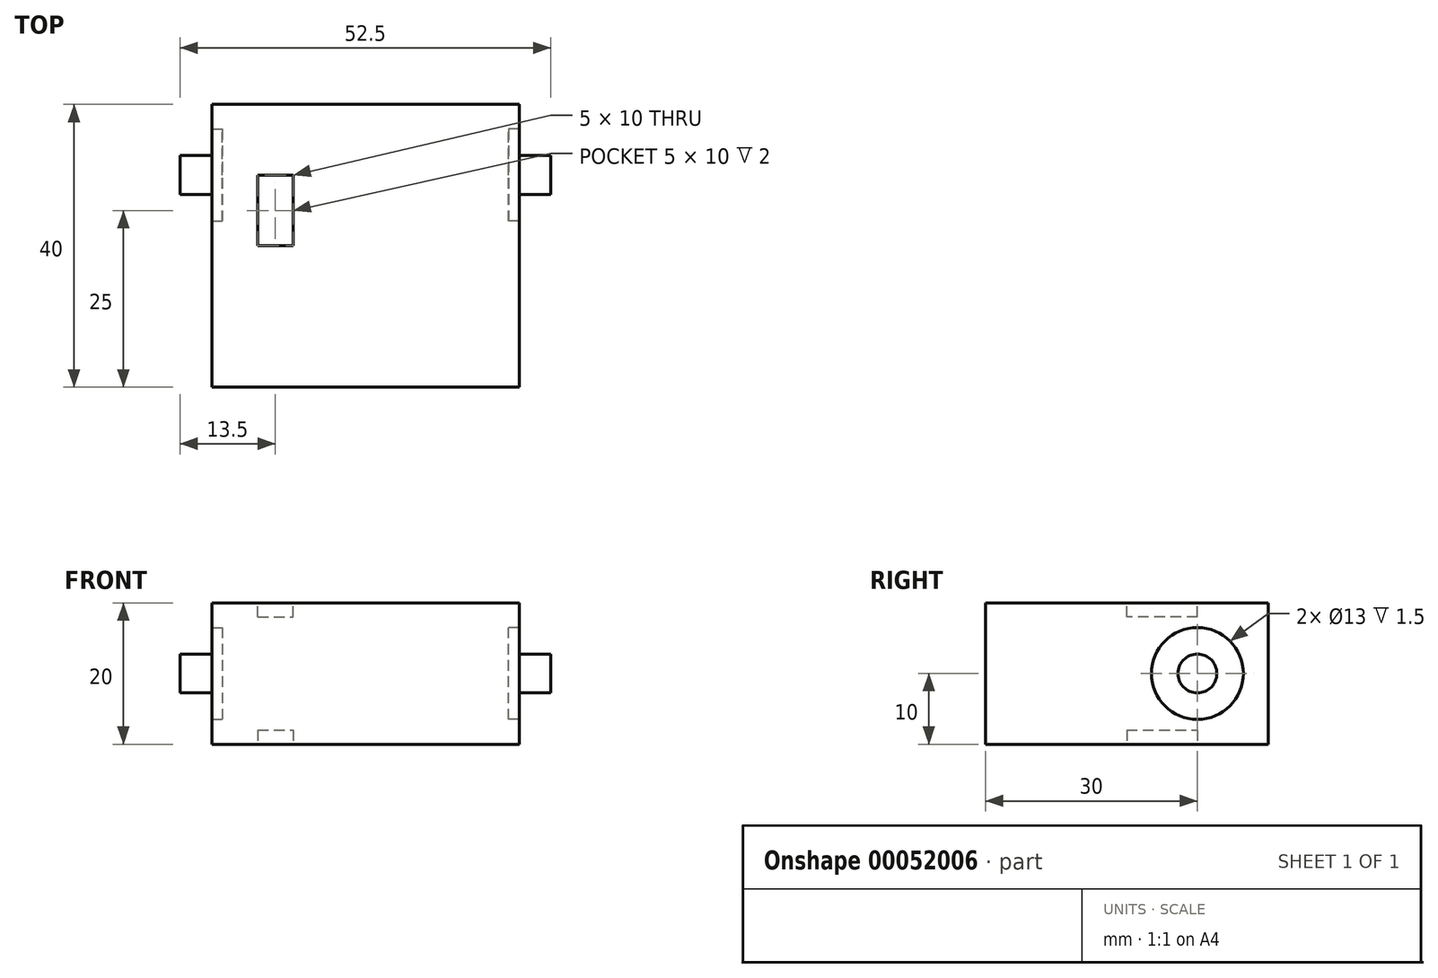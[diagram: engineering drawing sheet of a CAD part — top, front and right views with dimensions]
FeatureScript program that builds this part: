
annotation { "Feature Type Name" : "Feature", "Feature Type Description" : "" }
export const myFeature = defineFeature(function(context is Context, id is Id, definition is map)
    precondition{}
    {
        {
            var Q0;
            Q0=qCreatedBy(makeId("Top.planeOp"),FACE);
            var sketch = newSketch(context, id + "F0", { "sketchPlane" : qUnion([Q0])});
            skLineSegment(sketch, "E0.bottom", {"start": v(-20.25, 20) * mm, "end": v(20.25, 20) * mm});
            skLineSegment(sketch, "E0.top", {"start": v(-20.25, -20) * mm, "end": v(20.25, -20) * mm});
            skLineSegment(sketch, "E0.left", {"start": v(-20.25, 20) * mm, "end": v(-20.25, -20) * mm});
            skLineSegment(sketch, "E0.right", {"start": v(20.25, 20) * mm, "end": v(20.25, -20) * mm});
            skSolve(sketch);
        }
        {
            var Q0;
            Q0=makeQuery(id+"F0.imprint","IMPRINT",FACE,{"disambiguationData":[TD([[makeQuery(id+"F0.imprint","IMPRINT",EDGE,{"derivedFrom":sQuery(id+"F0.wireOp",EDGE,"E0.bottom")}),-1.0]])]});
            extrude(context, id + "F1", {"entities" : qUnion([Q0]), "endBound" : BoundingType.SYMMETRIC, "oppositeDirection" : true, "depth" : 20 * mm, "offsetDistance" : 25 * mm});
        }
        {
            var Q0;
            Q0=makeQuery(id+"F1.opExtrude","SWEPT_FACE",FACE,{"disambiguationData":[OSD([sQuery(id+"F0.wireOp",EDGE,"E0.left")])]});
            var sketch = newSketch(context, id + "F2", { "sketchPlane" : qUnion([Q0])});
            skLineSegment(sketch, "E1.bottom", {"start": v(-20, 10) * mm, "end": v(-10, 10) * mm});
            skLineSegment(sketch, "E1.top", {"start": v(-20, -10) * mm, "end": v(-10, -10) * mm});
            skLineSegment(sketch, "E1.left", {"start": v(-20, 10) * mm, "end": v(-20, -10) * mm});
            skLineSegment(sketch, "E1.right", {"start": v(-10, 10) * mm, "end": v(-10, -10) * mm});
            skPoint(sketch, "E2", {"position": v(-10, 0) * mm});
            skCircle(sketch, "E3", {"center": v(-10, 0) * mm, "radius": 6.5 * mm});
            skSolve(sketch);
        }
        {
            var Q0;
            {var subQ0=sQuery(id+"F2.wireOp",EDGE,"E3");var subQ1=sQuery(id+"F2.wireOp",EDGE,"E1.right");var subQ2=makeQuery(id+"F2.imprint","INTERSECT",VERTEX,{"disambiguationData":[OD(0.0)],"derivedFrom":[subQ1,subQ0]});Q0=makeQuery(id+"F2.imprint","IMPRINT",FACE,{"disambiguationData":[TD([[makeQuery(id+"F2.imprint","IMPRINT",EDGE,{"disambiguationData":[TD([[subQ2,-1.0]])],"derivedFrom":subQ1}),-1.0]])]});}
            var Q1;
            {var subQ0=sQuery(id+"F2.wireOp",EDGE,"E3");var subQ1=sQuery(id+"F2.wireOp",EDGE,"E1.right");var subQ2=makeQuery(id+"F2.imprint","INTERSECT",VERTEX,{"disambiguationData":[OD(0.0)],"derivedFrom":[subQ1,subQ0]});Q1=makeQuery(id+"F2.imprint","IMPRINT",FACE,{"disambiguationData":[TD([[makeQuery(id+"F2.imprint","IMPRINT",EDGE,{"disambiguationData":[TD([[subQ2,-1.0]])],"derivedFrom":subQ1}),1.0]])]});}
            extrude(context, id + "F3", {"entities" : qUnion([Q0, Q1]), "operationType" : NewBodyOperationType.ADD, "depth" : 1.5 * mm, "offsetDistance" : 25 * mm});
        }
        {
            var Q0;
            Q0=makeQuery(id+"F3.opExtrude","CAP_FACE",FACE,{"disambiguationData":[OSD([sQuery(id+"F2.wireOp",EDGE,"E3")])],"isStart":false});
            var sketch = newSketch(context, id + "F4", { "sketchPlane" : qUnion([Q0])});
            skCircle(sketch, "E4", {"center": v(-10, 0) * mm, "radius": 2.75 * mm});
            skSolve(sketch);
        }
        {
            var Q0;
            Q0=makeQuery(id+"F4.imprint","IMPRINT",FACE,{"disambiguationData":[TD([[makeQuery(id+"F4.imprint","IMPRINT",EDGE,{"derivedFrom":sQuery(id+"F4.wireOp",EDGE,"E4")}),1.0]])]});
            extrude(context, id + "F5", {"entities" : qUnion([Q0]), "operationType" : NewBodyOperationType.ADD, "depth" : 4.5 * mm, "offsetDistance" : 25 * mm});
        }
        {
            var Q0;
            Q0=makeQuery(id+"F1.opExtrude","SWEPT_FACE",FACE,{"disambiguationData":[OSD([sQuery(id+"F0.wireOp",EDGE,"E0.right")])]});
            var sketch = newSketch(context, id + "F6", { "sketchPlane" : qUnion([Q0])});
            skLineSegment(sketch, "E5.bottom", {"start": v(20, 10) * mm, "end": v(10, 10) * mm});
            skLineSegment(sketch, "E5.top", {"start": v(20, -10) * mm, "end": v(10, -10) * mm});
            skLineSegment(sketch, "E5.left", {"start": v(20, 10) * mm, "end": v(20, -10) * mm});
            skLineSegment(sketch, "E5.right", {"start": v(10, 10) * mm, "end": v(10, -10) * mm});
            skCircle(sketch, "E6", {"center": v(10, 0) * mm, "radius": 6.5 * mm});
            skSolve(sketch);
        }
        {
            var Q0;
            {var subQ0=sQuery(id+"F6.wireOp",EDGE,"E6");var subQ1=sQuery(id+"F6.wireOp",EDGE,"E5.right");var subQ2=makeQuery(id+"F6.imprint","INTERSECT",VERTEX,{"disambiguationData":[OD(0.0)],"derivedFrom":[subQ1,subQ0]});Q0=makeQuery(id+"F6.imprint","IMPRINT",FACE,{"disambiguationData":[TD([[makeQuery(id+"F6.imprint","IMPRINT",EDGE,{"disambiguationData":[TD([[subQ2,-1.0]])],"derivedFrom":subQ1}),1.0]])]});}
            var Q1;
            {var subQ0=sQuery(id+"F6.wireOp",EDGE,"E6");var subQ1=sQuery(id+"F6.wireOp",EDGE,"E5.right");var subQ2=makeQuery(id+"F6.imprint","INTERSECT",VERTEX,{"disambiguationData":[OD(0.0)],"derivedFrom":[subQ1,subQ0]});Q1=makeQuery(id+"F6.imprint","IMPRINT",FACE,{"disambiguationData":[TD([[makeQuery(id+"F6.imprint","IMPRINT",EDGE,{"disambiguationData":[TD([[subQ2,-1.0]])],"derivedFrom":subQ1}),-1.0]])]});}
            extrude(context, id + "F7", {"entities" : qUnion([Q0, Q1]), "operationType" : NewBodyOperationType.ADD, "depth" : 1.5 * mm});
        }
        {
            var Q0;
            Q0=makeQuery(id+"F7.opExtrude","CAP_FACE",FACE,{"disambiguationData":[OSD([sQuery(id+"F6.wireOp",EDGE,"E6")])],"isStart":false});
            var sketch = newSketch(context, id + "F8", { "sketchPlane" : qUnion([Q0])});
            skCircle(sketch, "E7", {"center": v(10, 0) * mm, "radius": 2.75 * mm});
            skSolve(sketch);
        }
        {
            var Q0;
            Q0=makeQuery(id+"F8.imprint","IMPRINT",FACE,{"disambiguationData":[TD([[makeQuery(id+"F8.imprint","IMPRINT",EDGE,{"derivedFrom":sQuery(id+"F8.wireOp",EDGE,"E7")}),1.0]])]});
            extrude(context, id + "F9", {"entities" : qUnion([Q0]), "operationType" : NewBodyOperationType.ADD, "depth" : 4.5 * mm});
        }
        {
            var Q0;
            Q0=makeQuery(id+"F1.opExtrude","CAP_FACE",FACE,{"disambiguationData":[OSD([sQuery(id+"F0.wireOp",EDGE,"E0.bottom"),sQuery(id+"F0.wireOp",EDGE,"E0.top"),sQuery(id+"F0.wireOp",EDGE,"E0.left"),sQuery(id+"F0.wireOp",EDGE,"E0.right")])],"isStart":false});
            var sketch = newSketch(context, id + "F10", { "sketchPlane" : qUnion([Q0])});
            skLineSegment(sketch, "E8.bottom", {"start": v(-15.25, 0) * mm, "end": v(-10.25, 0) * mm});
            skLineSegment(sketch, "E8.top", {"start": v(-15.25, -10) * mm, "end": v(-10.25, -10) * mm});
            skLineSegment(sketch, "E8.left", {"start": v(-15.25, 0) * mm, "end": v(-15.25, -10) * mm});
            skLineSegment(sketch, "E8.right", {"start": v(-10.25, 0) * mm, "end": v(-10.25, -10) * mm});
            skSolve(sketch);
        }
        {
            var Q0;
            Q0=makeQuery(id+"F10.imprint","IMPRINT",FACE,{"disambiguationData":[TD([[makeQuery(id+"F10.imprint","IMPRINT",EDGE,{"derivedFrom":sQuery(id+"F10.wireOp",EDGE,"E8.bottom")}),-1.0]])]});
            extrude(context, id + "F11", {"entities" : qUnion([Q0]), "operationType" : NewBodyOperationType.REMOVE, "oppositeDirection" : true, "depth" : 2 * mm});
        }
        {
            var Q0;
            Q0=makeQuery(id+"F1.opExtrude","CAP_FACE",FACE,{"disambiguationData":[OSD([sQuery(id+"F0.wireOp",EDGE,"E0.bottom"),sQuery(id+"F0.wireOp",EDGE,"E0.top"),sQuery(id+"F0.wireOp",EDGE,"E0.left"),sQuery(id+"F0.wireOp",EDGE,"E0.right")])],"isStart":true});
            var sketch = newSketch(context, id + "F12", { "sketchPlane" : qUnion([Q0])});
            skLineSegment(sketch, "E9.bottom", {"start": v(-15.25, 10) * mm, "end": v(-10.25, 10) * mm});
            skLineSegment(sketch, "E9.top", {"start": v(-15.25, 0) * mm, "end": v(-10.25, 0) * mm});
            skLineSegment(sketch, "E9.left", {"start": v(-15.25, 10) * mm, "end": v(-15.25, 0) * mm});
            skLineSegment(sketch, "E9.right", {"start": v(-10.25, 10) * mm, "end": v(-10.25, 0) * mm});
            skSolve(sketch);
        }
        {
            var Q0;
            Q0=makeQuery(id+"F12.imprint","IMPRINT",FACE,{"disambiguationData":[TD([[makeQuery(id+"F12.imprint","IMPRINT",EDGE,{"derivedFrom":sQuery(id+"F12.wireOp",EDGE,"E9.bottom")}),-1.0]])]});
            extrude(context, id + "F13", {"entities" : qUnion([Q0]), "operationType" : NewBodyOperationType.REMOVE, "oppositeDirection" : true, "depth" : 2 * mm});
        }
    });
